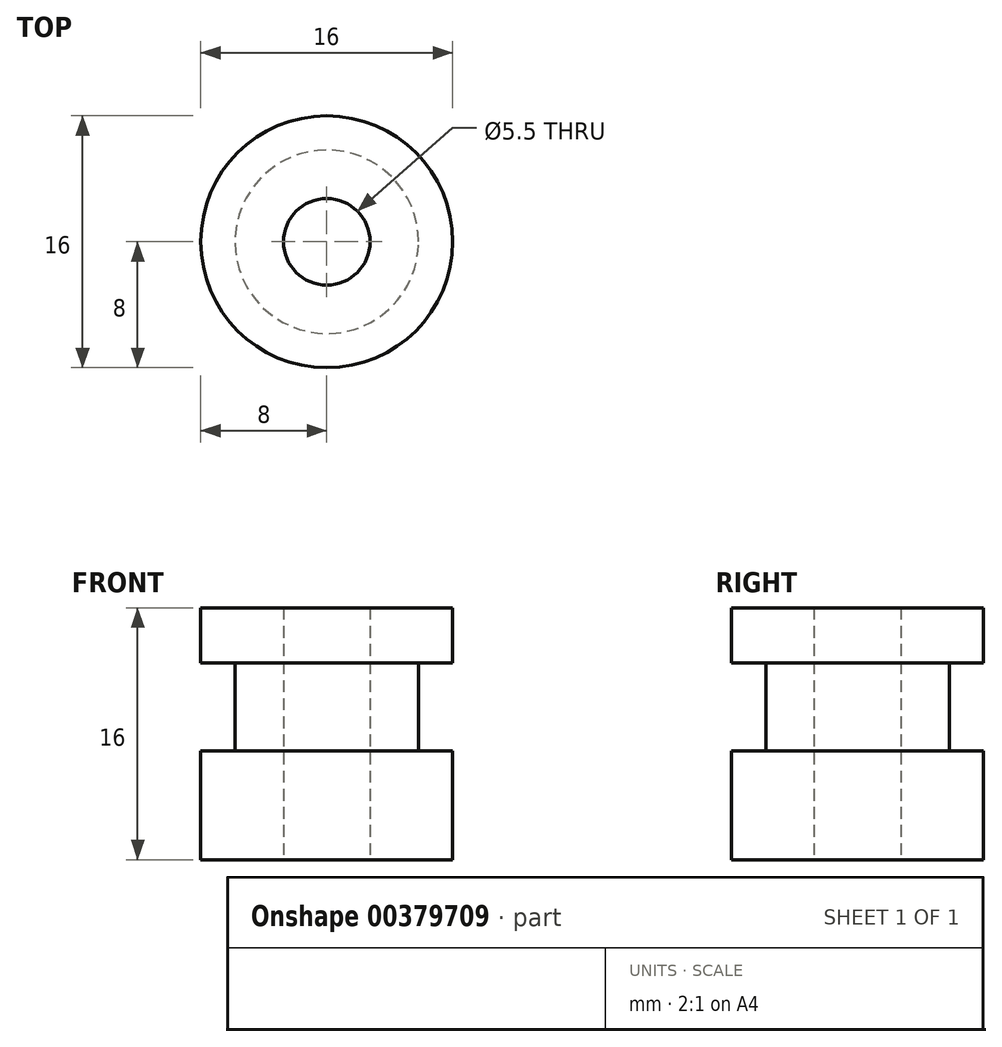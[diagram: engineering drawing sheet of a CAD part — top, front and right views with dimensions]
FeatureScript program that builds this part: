
annotation { "Feature Type Name" : "Feature", "Feature Type Description" : "" }
export const myFeature = defineFeature(function(context is Context, id is Id, definition is map)
    precondition{}
    {
        {
            var Q0;
            Q0=qCreatedBy(makeId("Top.planeOp"),FACE);
            var sketch = newSketch(context, id + "F0", { "sketchPlane" : qUnion([Q0])});
            skLineSegment(sketch, "E0.bottom", {"start": v(15, 12) * mm, "end": v(-15, 12) * mm});
            skLineSegment(sketch, "E0.top", {"start": v(15, -12) * mm, "end": v(-15, -12) * mm});
            skLineSegment(sketch, "E0.left", {"start": v(15, 12) * mm, "end": v(15, -12) * mm});
            skLineSegment(sketch, "E0.right", {"start": v(-15, 12) * mm, "end": v(-15, -12) * mm});
            skLineSegment(sketch, "E1.bottom", {"start": v(9, 6.7) * mm, "end": v(-9, 6.7) * mm, "construction": true});
            skLineSegment(sketch, "E1.top", {"start": v(9, -6.7) * mm, "end": v(-9, -6.7) * mm, "construction": true});
            skLineSegment(sketch, "E1.left", {"start": v(9, 6.7) * mm, "end": v(9, -6.7) * mm, "construction": true});
            skLineSegment(sketch, "E1.right", {"start": v(-9, 6.7) * mm, "end": v(-9, -6.7) * mm, "construction": true});
            skPoint(sketch, "E1.middle", {"position": v(0, 0) * mm});
            skSolve(sketch);
        }
        {
            var Q0;
            Q0=qSketchRegion(id+"F0",true);
            extrude(context, id + "F1", {"entities" : qUnion([Q0]), "oppositeDirection" : true, "depth" : 3 * mm});
        }
        {
            var Q0;
            Q0=sQuery(id+"F0.wireOp",VERTEX,"E1.right.start");
            var Q1;
            Q1=sQuery(id+"F0.wireOp",VERTEX,"E1.left.start");
            var Q2;
            Q2=makeQuery(id+"F1.opExtrude","SWEPT_BODY",BODY,{"disambiguationData":[OSD([sQuery(id+"F0.wireOp",EDGE,"E0.bottom"),sQuery(id+"F0.wireOp",EDGE,"E0.top"),sQuery(id+"F0.wireOp",EDGE,"E0.left"),sQuery(id+"F0.wireOp",EDGE,"E0.right")])]});
            hole(context, id + "F2", {"style" : HoleStyle.SIMPLE, "endStyle" : HoleEndStyle.THROUGH, "standardTappedOrClearance" : lookupTablePath({ "standard" : "ISO", "fit" : "Normal", "size" : "M3", "type" : "Clearance" }), "standardBlindInLast" : lookupTablePath({ "fit" : "Standard", "standard" : "ISO", "size" : "M3", "type" : "Clearance" }), "holeDiameter" : 3.3 * mm, "isTappedThrough" : true, "tappedDepth" : 12 * mm, "tapClearance" : 3, "startFromSketch" : true, "locations" : qUnion([Q0, Q1]), "scope" : qUnion([Q2])});
        }
        {
            var Q0;
            Q0=makeQuery(id+"F0.imprint","IMPRINT",FACE,{"disambiguationData":[TD([[makeQuery(id+"F0.imprint","IMPRINT",EDGE,{"derivedFrom":sQuery(id+"F0.wireOp",EDGE,"E0.bottom")}),1.0]])]});
            var sketch = newSketch(context, id + "F3", { "sketchPlane" : qUnion([Q0])});
            skCircle(sketch, "E2", {"center": v(0, 0) * mm, "radius": 8 * mm});
            skSolve(sketch);
        }
        {
            var Q0;
            Q0=makeQuery(id+"F3.imprint","IMPRINT",FACE,{"disambiguationData":[TD([[makeQuery(id+"F3.imprint","IMPRINT",EDGE,{"derivedFrom":sQuery(id+"F3.wireOp",EDGE,"E2")}),1.0]])]});
            extrude(context, id + "F4", {"entities" : qUnion([Q0]), "operationType" : NewBodyOperationType.ADD, "depth" : 16 * mm});
        }
        {
            var Q0;
            Q0=qCreatedBy(makeId("Top.planeOp"),FACE);
            cPlane(context, id + "F5", {"entities" : qUnion([Q0]), "cplaneType" : CPlaneType.OFFSET, "offset" : 16 * mm, "width" : 150 * mm, "height" : 150 * mm});
        }
        {
            var Q0;
            Q0=qCreatedBy(makeId("Front.planeOp"),FACE);
            var sketch = newSketch(context, id + "F6", { "sketchPlane" : qUnion([Q0])});
            skLineSegment(sketch, "E3.bottom", {"start": v(-8.03, 12.5) * mm, "end": v(-5.83, 12.5) * mm});
            skLineSegment(sketch, "E3.top", {"start": v(-8.03, 6.9) * mm, "end": v(-5.83, 6.9) * mm});
            skLineSegment(sketch, "E3.left", {"start": v(-8.03, 12.5) * mm, "end": v(-8.03, 6.9) * mm});
            skLineSegment(sketch, "E3.right", {"start": v(-5.83, 12.5) * mm, "end": v(-5.83, 6.9) * mm});
            skSolve(sketch);
        }
        {
            var Q0;
            Q0=qCreatedBy(makeId("Front.planeOp"),FACE);
            var sketch = newSketch(context, id + "F7", { "sketchPlane" : qUnion([Q0])});
            skLineSegment(sketch, "E4", {"start": v(0, 0) * mm, "end": v(0, 35.9) * mm, "construction": true});
            skSolve(sketch);
        }
        {
            var Q0;
            Q0=makeQuery(id+"F6.imprint","IMPRINT",FACE,{"disambiguationData":[TD([[makeQuery(id+"F6.imprint","IMPRINT",EDGE,{"derivedFrom":sQuery(id+"F6.wireOp",EDGE,"E3.bottom")}),-1.0]])]});
            var Q1;
            Q1=sQuery(id+"F7.wireOp",EDGE,"E4");
            var Q2;
            Q2=sQuery(id+"F7.wireOp",EDGE,"E4");
            revolve(context, id + "F8", {"operationType" : NewBodyOperationType.REMOVE, "entities" : qUnion([Q0]), "surfaceEntities" : qUnion([Q1]), "axis" : qUnion([Q2]), "revolveType" : RevolveType.FULL, "oppositeDirection" : true});
        }
        {
            var Q0;
            Q0=makeQuery(id+"F1.opExtrude","CAP_FACE",FACE,{"disambiguationData":[OSD([sQuery(id+"F0.wireOp",EDGE,"E0.bottom"),sQuery(id+"F0.wireOp",EDGE,"E0.top"),sQuery(id+"F0.wireOp",EDGE,"E0.left"),sQuery(id+"F0.wireOp",EDGE,"E0.right")])],"isStart":false});
            var sketch = newSketch(context, id + "F9", { "sketchPlane" : qUnion([Q0])});
            skPoint(sketch, "E5", {"position": v(0, 0) * mm});
            skSolve(sketch);
        }
        {
            var Q0;
            Q0=sQuery(id+"F9.wireOp",VERTEX,"E5");
            var Q1;
            Q1=makeQuery(id+"F1.opExtrude","SWEPT_BODY",BODY,{"disambiguationData":[OSD([sQuery(id+"F0.wireOp",EDGE,"E0.bottom"),sQuery(id+"F0.wireOp",EDGE,"E0.top"),sQuery(id+"F0.wireOp",EDGE,"E0.left"),sQuery(id+"F0.wireOp",EDGE,"E0.right")])]});
            hole(context, id + "F10", {"style" : HoleStyle.SIMPLE, "endStyle" : HoleEndStyle.THROUGH, "holeDiameter" : 5.5 * mm, "isTappedThrough" : true, "tappedDepth" : 12 * mm, "tapClearance" : 3, "startFromSketch" : true, "locations" : qUnion([Q0]), "scope" : qUnion([Q1]), "majorDiameter" : 5 * mm});
        }
        {
            var Q0;
            Q0=makeQuery(id+"F1.opExtrude","SWEPT_EDGE",EDGE,{"disambiguationData":[OSD([sQuery(id+"F0.wireOp",EDGE,"E0.top"),sQuery(id+"F0.wireOp",EDGE,"E0.left")])]});
            var Q1;
            Q1=makeQuery(id+"F1.opExtrude","SWEPT_EDGE",EDGE,{"disambiguationData":[OSD([sQuery(id+"F0.wireOp",EDGE,"E0.bottom"),sQuery(id+"F0.wireOp",EDGE,"E0.left")])]});
            var Q2;
            Q2=makeQuery(id+"F1.opExtrude","SWEPT_EDGE",EDGE,{"disambiguationData":[OSD([sQuery(id+"F0.wireOp",EDGE,"E0.bottom"),sQuery(id+"F0.wireOp",EDGE,"E0.right")])]});
            var Q3;
            Q3=makeQuery(id+"F1.opExtrude","SWEPT_EDGE",EDGE,{"disambiguationData":[OSD([sQuery(id+"F0.wireOp",EDGE,"E0.top"),sQuery(id+"F0.wireOp",EDGE,"E0.right")])]});
            fillet(context, id + "F11", {"entities" : qUnion([Q0, Q1, Q2, Q3]), "radius" : 5 * mm, "tangentPropagation" : true, "allowEdgeOverflow" : false});
        }
        {
            var Q0;
            Q0=qCreatedBy(makeId("Front.planeOp"),FACE);
            var sketch = newSketch(context, id + "F12", { "sketchPlane" : qUnion([Q0])});
            skLineSegment(sketch, "E6.bottom", {"start": v(-17.62, 0) * mm, "end": v(17.41, 0) * mm});
            skLineSegment(sketch, "E6.top", {"start": v(-17.62, -6.42) * mm, "end": v(17.41, -6.42) * mm});
            skLineSegment(sketch, "E6.left", {"start": v(-17.62, 0) * mm, "end": v(-17.62, -6.42) * mm});
            skLineSegment(sketch, "E6.right", {"start": v(17.41, 0) * mm, "end": v(17.41, -6.42) * mm});
            skSolve(sketch);
        }
        {
            var Q0;
            Q0 = qSketchRegion(id + "F12", true);
            extrude(context, id + "F13", {"entities" : qUnion([Q0]), "operationType" : NewBodyOperationType.REMOVE, "oppositeDirection" : true, "depth" : 25 * mm, "offsetDistance" : 25 * mm, "hasSecondDirection" : true, "secondDirectionOppositeDirection" : false, "secondDirectionDepth" : 25 * mm});
        }
    });
